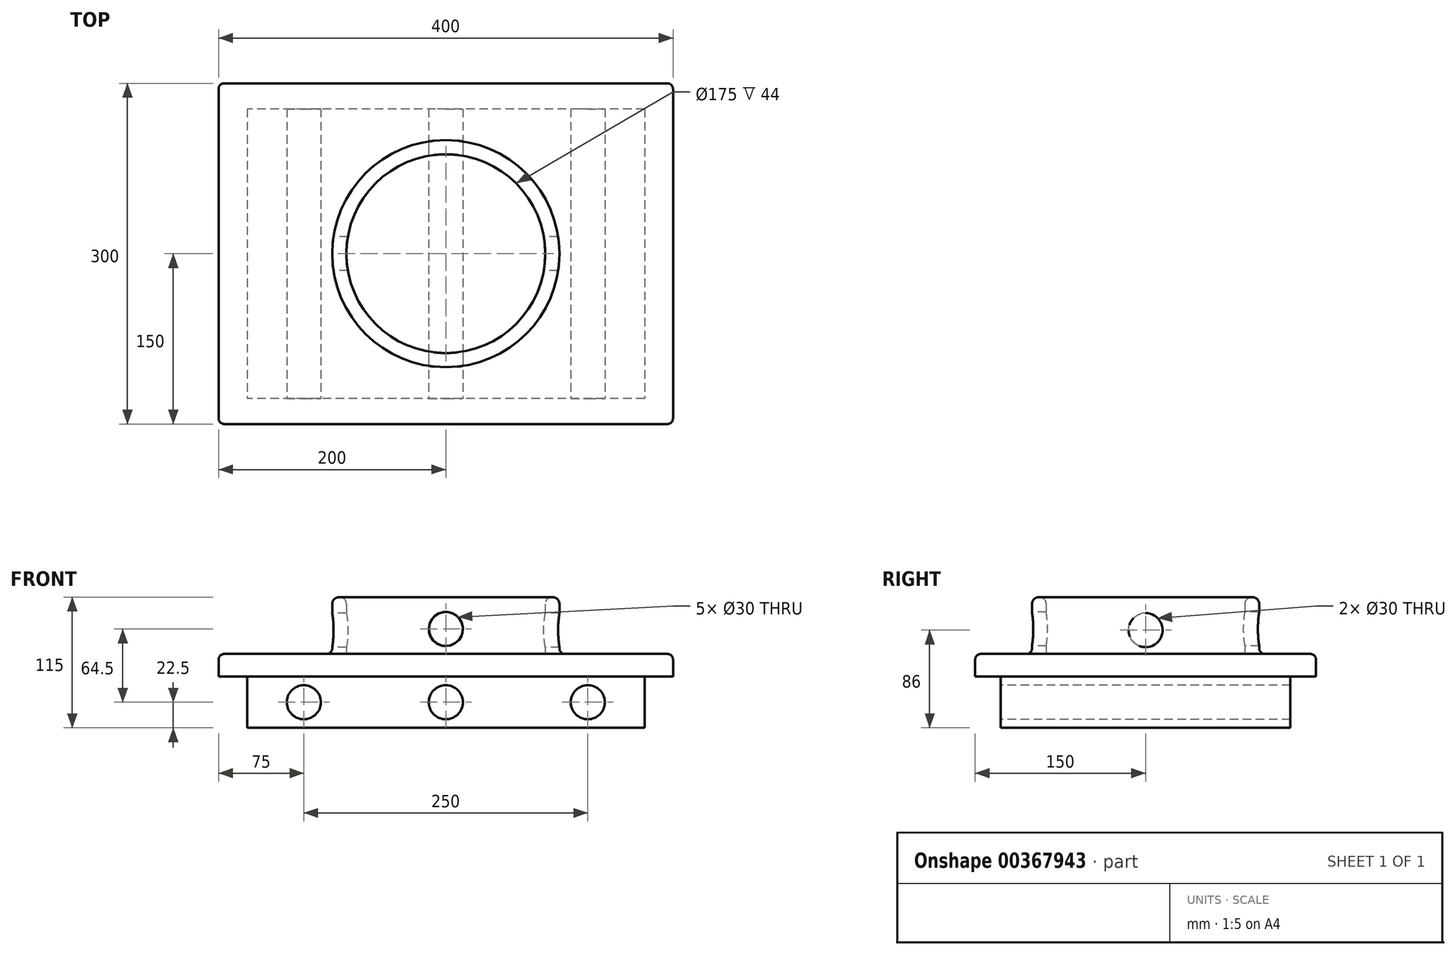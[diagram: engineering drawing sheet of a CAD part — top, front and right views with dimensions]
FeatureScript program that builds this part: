
annotation { "Feature Type Name" : "Feature", "Feature Type Description" : "" }
export const myFeature = defineFeature(function(context is Context, id is Id, definition is map)
    precondition{}
    {
        {
            var Q0;
            Q0=qCreatedBy(makeId("Top.planeOp"),FACE);
            var sketch = newSketch(context, id + "F0", { "sketchPlane" : qUnion([Q0])});
            skLineSegment(sketch, "E0.bottom", {"start": v(200, -150) * mm, "end": v(-200, -150) * mm});
            skLineSegment(sketch, "E0.top", {"start": v(200, 150) * mm, "end": v(-200, 150) * mm});
            skLineSegment(sketch, "E0.left", {"start": v(200, -150) * mm, "end": v(200, 150) * mm});
            skLineSegment(sketch, "E0.right", {"start": v(-200, -150) * mm, "end": v(-200, 150) * mm});
            skPoint(sketch, "E0.middle", {"position": v(0, 0) * mm});
            skSolve(sketch);
        }
        {
            var Q0;
            Q0 = qSketchRegion(id + "F0", true);
            extrude(context, id + "F1", {"entities" : qUnion([Q0]), "depth" : 20 * mm});
        }
        {
            var Q0;
            Q0=makeQuery(id+"F1.opExtrude","CAP_FACE",FACE,{"disambiguationData":[OSD([sQuery(id+"F0.wireOp",EDGE,"E0.bottom"),sQuery(id+"F0.wireOp",EDGE,"E0.top"),sQuery(id+"F0.wireOp",EDGE,"E0.left"),sQuery(id+"F0.wireOp",EDGE,"E0.right")])],"isStart":false});
            var sketch = newSketch(context, id + "F2", { "sketchPlane" : qUnion([Q0])});
            skCircle(sketch, "E1", {"center": v(0, 0) * mm, "radius": 100 * mm});
            skCircle(sketch, "E2", {"center": v(0, 0) * mm, "radius": 87.5 * mm});
            skSolve(sketch);
        }
        {
            var Q0;
            Q0 = qSketchRegion(id + "F2", true);
            extrude(context, id + "F3", {"entities" : qUnion([Q0]), "operationType" : NewBodyOperationType.ADD, "depth" : 50 * mm});
        }
        {
            var Q0;
            Q0=makeQuery(id+"F3.opExtrude","CAP_EDGE",EDGE,{"disambiguationData":[OSD([sQuery(id+"F2.wireOp",EDGE,"E1")])],"isStart":false});
            var Q1;
            Q1=makeQuery(id+"F3.opExtrude","CAP_EDGE",EDGE,{"disambiguationData":[OSD([sQuery(id+"F2.wireOp",EDGE,"E2")])],"isStart":false});
            fillet(context, id + "F4", {"entities" : qUnion([Q0, Q1]), "radius" : 6 * mm, "tangentPropagation" : true, "allowEdgeOverflow" : false});
        }
        {
            var Q0;
            Q0=qCreatedBy(makeId("Front.planeOp"),FACE);
            cPlane(context, id + "F5", {"entities" : qUnion([Q0]), "cplaneType" : CPlaneType.OFFSET, "offset" : 100 * mm, "width" : 150 * mm, "height" : 150 * mm});
        }
        {
            var Q0;
            Q0=qCreatedBy(id+"F5.planeOp",FACE);
            var sketch = newSketch(context, id + "F6", { "sketchPlane" : qUnion([Q0])});
            skCircle(sketch, "E3", {"center": v(0, 42) * mm, "radius": 15 * mm});
            skSolve(sketch);
        }
        {
            var Q0;
            Q0 = qSketchRegion(id + "F6", true);
            extrude(context, id + "F7", {"entities" : qUnion([Q0]), "operationType" : NewBodyOperationType.REMOVE, "oppositeDirection" : true, "depth" : 200 * mm});
        }
        {
            var Q0;
            Q0=qCreatedBy(makeId("Right.planeOp"),FACE);
            cPlane(context, id + "F8", {"entities" : qUnion([Q0]), "cplaneType" : CPlaneType.OFFSET, "offset" : 100 * mm, "oppositeDirection" : true, "width" : 150 * mm, "height" : 150 * mm});
        }
        {
            var Q0;
            Q0=qCreatedBy(id+"F8.planeOp",FACE);
            var sketch = newSketch(context, id + "F9", { "sketchPlane" : qUnion([Q0])});
            skCircle(sketch, "E4", {"center": v(0, 41) * mm, "radius": 15 * mm});
            skSolve(sketch);
        }
        {
            var Q0;
            Q0=makeQuery(id+"F9.imprint","IMPRINT",FACE,{"disambiguationData":[TD([[makeQuery(id+"F9.imprint","IMPRINT",EDGE,{"derivedFrom":sQuery(id+"F9.wireOp",EDGE,"E4")}),1.0]])]});
            extrude(context, id + "F10", {"entities" : qUnion([Q0]), "operationType" : NewBodyOperationType.REMOVE, "depth" : 200 * mm});
        }
        {
            var Q0;
            Q0=makeQuery(id+"F1.opExtrude","CAP_FACE",FACE,{"disambiguationData":[OSD([sQuery(id+"F0.wireOp",EDGE,"E0.bottom"),sQuery(id+"F0.wireOp",EDGE,"E0.top"),sQuery(id+"F0.wireOp",EDGE,"E0.left"),sQuery(id+"F0.wireOp",EDGE,"E0.right")])],"isStart":true});
            var sketch = newSketch(context, id + "F11", { "sketchPlane" : qUnion([Q0])});
            skLineSegment(sketch, "E5.bottom", {"start": v(175, -127.5) * mm, "end": v(-175, -127.5) * mm});
            skLineSegment(sketch, "E5.top", {"start": v(175, 127.5) * mm, "end": v(-175, 127.5) * mm});
            skLineSegment(sketch, "E5.left", {"start": v(175, -127.5) * mm, "end": v(175, 127.5) * mm});
            skLineSegment(sketch, "E5.right", {"start": v(-175, -127.5) * mm, "end": v(-175, 127.5) * mm});
            skPoint(sketch, "E5.middle", {"position": v(0, 0) * mm});
            skSolve(sketch);
        }
        {
            var Q0;
            Q0 = qSketchRegion(id + "F11", true);
            extrude(context, id + "F12", {"entities" : qUnion([Q0]), "operationType" : NewBodyOperationType.ADD, "depth" : 45 * mm});
        }
        {
            var Q0;
            Q0=makeQuery(id+"F12.opExtrude","SWEPT_FACE",FACE,{"disambiguationData":[OSD([sQuery(id+"F11.wireOp",EDGE,"E5.top")])]});
            var sketch = newSketch(context, id + "F13", { "sketchPlane" : qUnion([Q0])});
            skCircle(sketch, "E6", {"center": v(-125, -22.5) * mm, "radius": 15 * mm});
            skCircle(sketch, "E7", {"center": v(125, -22.5) * mm, "radius": 15 * mm});
            skCircle(sketch, "E8", {"center": v(0, -22.5) * mm, "radius": 15 * mm});
            skSolve(sketch);
        }
        {
            var Q0;
            Q0=makeQuery(id+"F13.imprint","IMPRINT",FACE,{"disambiguationData":[TD([[makeQuery(id+"F13.imprint","IMPRINT",EDGE,{"derivedFrom":sQuery(id+"F13.wireOp",EDGE,"E6")}),1.0]])]});
            var Q1;
            Q1=sQuery(id+"F13.wireOp",EDGE,"E6");
            extrude(context, id + "F14", {"entities" : qUnion([Q0]), "operationType" : NewBodyOperationType.REMOVE, "surfaceEntities" : qUnion([Q1]), "oppositeDirection" : true, "depth" : 255 * mm});
        }
        {
            var Q0;
            Q0 = qSketchRegion(id + "F13", true);
            extrude(context, id + "F15", {"entities" : qUnion([Q0]), "operationType" : NewBodyOperationType.REMOVE, "oppositeDirection" : true, "depth" : 256 * mm});
        }
        {
            var Q0;
            {var subQ0=sQuery(id+"F0.wireOp",EDGE,"E0.left");var subQ1=sQuery(id+"F0.wireOp",EDGE,"E0.top");var subQ2=sQuery(id+"F0.wireOp",EDGE,"E0.right");var subQ3=sQuery(id+"F0.wireOp",EDGE,"E0.bottom");Q0=makeQuery(id+"F3.boolean.opBoolean","SPLIT",FACE,{"disambiguationData":[TD([makeQuery(id+"F1.opExtrude","SWEPT_FACE",FACE,{"disambiguationData":[OSD([subQ3])]})])],"derivedFrom":makeQuery(id+"F1.opExtrude","CAP_FACE",FACE,{"disambiguationData":[OSD([subQ3,subQ1,subQ0,subQ2])],"isStart":false})});}
            var Q1;
            Q1=makeQuery(id+"F1.opExtrude","SWEPT_EDGE",EDGE,{"disambiguationData":[OSD([sQuery(id+"F0.wireOp",EDGE,"E0.bottom"),sQuery(id+"F0.wireOp",EDGE,"E0.right")])]});
            var Q2;
            Q2=makeQuery(id+"F1.opExtrude","CAP_EDGE",EDGE,{"disambiguationData":[OSD([sQuery(id+"F0.wireOp",EDGE,"E0.bottom")])],"isStart":false});
            var Q3;
            Q3=makeQuery(id+"F1.opExtrude","SWEPT_EDGE",EDGE,{"disambiguationData":[OSD([sQuery(id+"F0.wireOp",EDGE,"E0.bottom"),sQuery(id+"F0.wireOp",EDGE,"E0.left")])]});
            var Q4;
            Q4=makeQuery(id+"F1.opExtrude","SWEPT_EDGE",EDGE,{"disambiguationData":[OSD([sQuery(id+"F0.wireOp",EDGE,"E0.top"),sQuery(id+"F0.wireOp",EDGE,"E0.left")])]});
            var Q5;
            Q5=makeQuery(id+"F1.opExtrude","SWEPT_EDGE",EDGE,{"disambiguationData":[OSD([sQuery(id+"F0.wireOp",EDGE,"E0.top"),sQuery(id+"F0.wireOp",EDGE,"E0.right")])]});
            fillet(context, id + "F16", {"entities" : qUnion([Q0, Q1, Q2, Q3, Q4, Q5]), "radius" : 5 * mm, "tangentPropagation" : true, "allowEdgeOverflow" : false});
        }
    });
